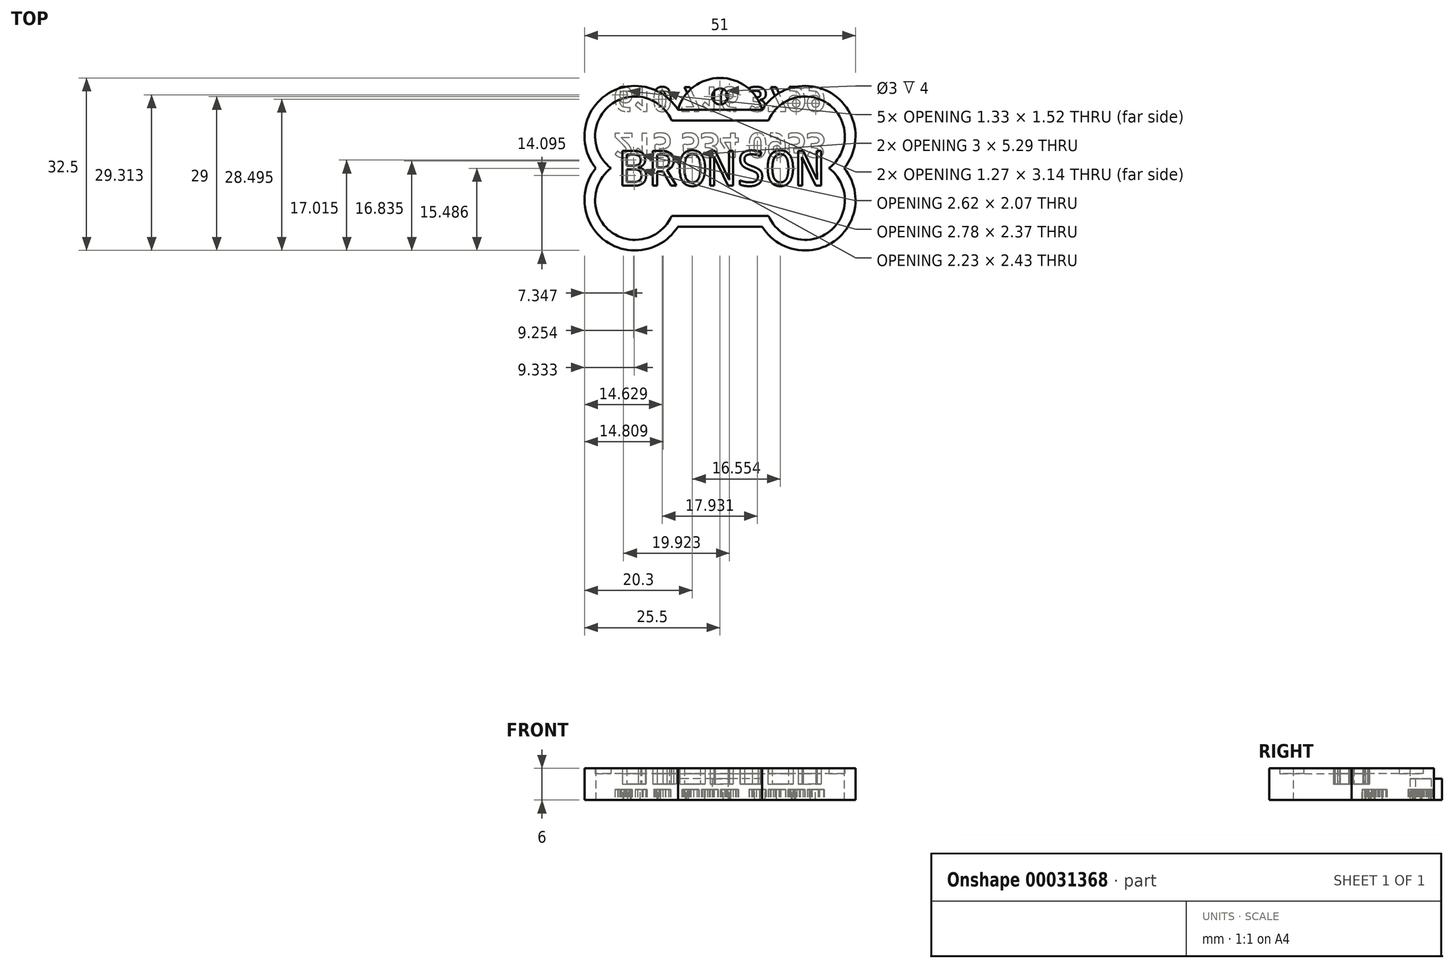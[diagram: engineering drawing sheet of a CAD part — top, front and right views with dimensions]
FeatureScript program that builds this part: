
annotation { "Feature Type Name" : "Feature", "Feature Type Description" : "" }
export const myFeature = defineFeature(function(context is Context, id is Id, definition is map)
    precondition{}
    {
        {
            var Q0;
            Q0=qCreatedBy(makeId("Top.planeOp"),FACE);
            var sketch = newSketch(context, id + "F0", { "sketchPlane" : qUnion([Q0])});
            skArc(sketch, "E0", {"start": v(-9.13, 9) * mm, "mid": v(-20.65, 11.88) * mm, "end": v(-20.5, 0) * mm});
            skLineSegment(sketch, "E1", {"start": v(0, 0) * mm, "end": v(0, -53.38) * mm, "construction": true});
            skLineSegment(sketch, "E2", {"start": v(0, 0) * mm, "end": v(-83.47, 0) * mm, "construction": true});
            skLineSegment(sketch, "E3", {"start": v(-9.13, 9) * mm, "end": v(0, 9) * mm});
            skArc(sketch, "E4.MirrorC", {"start": v(-9.13, -9) * mm, "mid": v(-20.65, -11.88) * mm, "end": v(-20.5, 0) * mm});
            skLineSegment(sketch, "E5.MirrorCS", {"start": v(-9.13, -9) * mm, "end": v(0, -9) * mm});
            skLineSegment(sketch, "E6.MirrorCS", {"start": v(9.13, 9) * mm, "end": v(0, 9) * mm});
            skLineSegment(sketch, "E7.MirrorCS", {"start": v(9.13, -9) * mm, "end": v(0, -9) * mm});
            skArc(sketch, "E8.MirrorC", {"start": v(9.13, -9) * mm, "mid": v(20.65, -11.88) * mm, "end": v(20.5, 0) * mm});
            skArc(sketch, "E9.MirrorC", {"start": v(9.13, 9) * mm, "mid": v(20.65, 11.88) * mm, "end": v(20.5, 0) * mm});
            skArc(sketch, "E10.0", {"start": v(7.92, 11) * mm, "mid": v(21.51, 13.74) * mm, "end": v(23.37, 0) * mm});
            skArc(sketch, "E10.1", {"start": v(7.92, -11) * mm, "mid": v(21.51, -13.74) * mm, "end": v(23.37, 0) * mm});
            skLineSegment(sketch, "E10.2", {"start": v(7.92, -11) * mm, "end": v(0, -11) * mm});
            skLineSegment(sketch, "E10.3", {"start": v(-7.92, -11) * mm, "end": v(0, -11) * mm});
            skArc(sketch, "E10.4", {"start": v(-7.92, -11) * mm, "mid": v(-21.51, -13.74) * mm, "end": v(-23.37, 0) * mm});
            skLineSegment(sketch, "E10.5", {"start": v(7.92, 11) * mm, "end": v(0, 11) * mm});
            skArc(sketch, "E10.6", {"start": v(-7.92, 11) * mm, "mid": v(-21.51, 13.74) * mm, "end": v(-23.37, 0) * mm});
            skLineSegment(sketch, "E10.7", {"start": v(-7.92, 11) * mm, "end": v(0, 11) * mm});
            skArc(sketch, "E11", {"start": v(7.92, 11) * mm, "mid": v(0, 17) * mm, "end": v(-7.92, 11) * mm});
            skLineSegment(sketch, "E12.bottom", {"start": v(-16, 6) * mm, "end": v(16, 6) * mm, "construction": true});
            skLineSegment(sketch, "E12.top", {"start": v(-16, -6) * mm, "end": v(16, -6) * mm, "construction": true});
            skLineSegment(sketch, "E12.left", {"start": v(-16, 6) * mm, "end": v(-16, -6) * mm, "construction": true});
            skLineSegment(sketch, "E12.right", {"start": v(16, 6) * mm, "end": v(16, -6) * mm, "construction": true});
            skPoint(sketch, "E13", {"position": v(0, 13.5) * mm});
            skSolve(sketch);
        }
        {
            var Q0;
            Q0=makeQuery(id+"F0.imprint","IMPRINT",FACE,{"disambiguationData":[TD([[makeQuery(id+"F0.imprint","IMPRINT",EDGE,{"derivedFrom":sQuery(id+"F0.wireOp",EDGE,"E0")}),-1.0]])]});
            extrude(context, id + "F1", {"entities" : qUnion([Q0]), "offsetDistance" : 25 * mm, "depth" : 6 * mm});
        }
        {
            var Q0;
            Q0=makeQuery(id+"F0.imprint","IMPRINT",FACE,{"disambiguationData":[TD([[makeQuery(id+"F0.imprint","IMPRINT",EDGE,{"derivedFrom":sQuery(id+"F0.wireOp",EDGE,"E10.5")}),-1.0]])]});
            extrude(context, id + "F2", {"entities" : qUnion([Q0]), "operationType" : NewBodyOperationType.ADD, "offsetDistance" : 25 * mm, "depth" : 4 * mm});
        }
        {
            var Q0;
            Q0=sQuery(id+"F0.wireOp",VERTEX,"E13");
            var Q1;
            Q1=makeQuery(id+"F1.opExtrude","SWEPT_BODY",BODY,{"disambiguationData":[OSD([sQuery(id+"F0.wireOp",EDGE,"E0"),sQuery(id+"F0.wireOp",EDGE,"E3"),sQuery(id+"F0.wireOp",EDGE,"E4.MirrorC"),sQuery(id+"F0.wireOp",EDGE,"E5.MirrorCS"),sQuery(id+"F0.wireOp",EDGE,"E6.MirrorCS"),sQuery(id+"F0.wireOp",EDGE,"E7.MirrorCS"),sQuery(id+"F0.wireOp",EDGE,"E8.MirrorC"),sQuery(id+"F0.wireOp",EDGE,"E9.MirrorC"),sQuery(id+"F0.wireOp",EDGE,"E10.0"),sQuery(id+"F0.wireOp",EDGE,"E10.1"),sQuery(id+"F0.wireOp",EDGE,"E10.2"),sQuery(id+"F0.wireOp",EDGE,"E10.3"),sQuery(id+"F0.wireOp",EDGE,"E10.4"),sQuery(id+"F0.wireOp",EDGE,"E10.6"),sQuery(id+"F0.wireOp",EDGE,"E11")])]});
            hole(context, id + "F3", {"style" : HoleStyle.SIMPLE, "holeDiameter" : 3 * mm, "endStyle" : HoleEndStyle.THROUGH, "oppositeDirection" : true, "locations" : qUnion([Q0]), "scope" : qUnion([Q1])});
        }
        {
            var Q0;
            Q0=makeQuery(id+"F0.imprint","IMPRINT",FACE,{"disambiguationData":[TD([[makeQuery(id+"F0.imprint","IMPRINT",EDGE,{"derivedFrom":sQuery(id+"F0.wireOp",EDGE,"E0")}),1.0]])]});
            extrude(context, id + "F4", {"entities" : qUnion([Q0]), "operationType" : NewBodyOperationType.ADD, "offsetDistance" : 25 * mm, "depth" : 3 * mm});
        }
        {
            var Q0;
            Q0=makeQuery(id+"F4.opExtrude","CAP_FACE",FACE,{"disambiguationData":[OSD([sQuery(id+"F0.wireOp",EDGE,"E0"),sQuery(id+"F0.wireOp",EDGE,"E3"),sQuery(id+"F0.wireOp",EDGE,"E4.MirrorC"),sQuery(id+"F0.wireOp",EDGE,"E5.MirrorCS"),sQuery(id+"F0.wireOp",EDGE,"E6.MirrorCS"),sQuery(id+"F0.wireOp",EDGE,"E7.MirrorCS"),sQuery(id+"F0.wireOp",EDGE,"E8.MirrorC"),sQuery(id+"F0.wireOp",EDGE,"E9.MirrorC")])],"isStart":false});
            var sketch = newSketch(context, id + "F5", { "sketchPlane" : qUnion([Q0])});
            skText(sketch, "E14", { "text": "BRONSON", "fontName": "DroidSansMono.ttf"});
            skPoint(sketch, "E15", {"position": v(-19, 0) * mm});
            const initialGuessF5  = {"E14": [-0.019, -0.0033, 1, 0, 0.00662]};
            skSetInitialGuess(sketch, initialGuessF5);
            skSolve(sketch);
        }
        {
            var Q0;
            Q0=makeQuery(id+"F5.imprint","IMPRINT",FACE,{"disambiguationData":[TD([[makeQuery(id+"F5.imprint","IMPRINT",EDGE,{"derivedFrom":sQuery(id+"F5.wireOp",EDGE,"E14.sketch_text.stroke-0")}),1.0]])]});
            var Q1;
            Q1=makeQuery(id+"F1.opExtrude","CAP_FACE",FACE,{"disambiguationData":[OSD([sQuery(id+"F0.wireOp",EDGE,"E0"),sQuery(id+"F0.wireOp",EDGE,"E3"),sQuery(id+"F0.wireOp",EDGE,"E4.MirrorC"),sQuery(id+"F0.wireOp",EDGE,"E5.MirrorCS"),sQuery(id+"F0.wireOp",EDGE,"E6.MirrorCS"),sQuery(id+"F0.wireOp",EDGE,"E7.MirrorCS"),sQuery(id+"F0.wireOp",EDGE,"E8.MirrorC"),sQuery(id+"F0.wireOp",EDGE,"E9.MirrorC"),sQuery(id+"F0.wireOp",EDGE,"E10.0"),sQuery(id+"F0.wireOp",EDGE,"E10.1"),sQuery(id+"F0.wireOp",EDGE,"E10.2"),sQuery(id+"F0.wireOp",EDGE,"E10.3"),sQuery(id+"F0.wireOp",EDGE,"E10.4"),sQuery(id+"F0.wireOp",EDGE,"E10.5"),sQuery(id+"F0.wireOp",EDGE,"E10.6"),sQuery(id+"F0.wireOp",EDGE,"E10.7")])],"isStart":false});
            extrude(context, id + "F6", {"entities" : qUnion([Q0]), "operationType" : NewBodyOperationType.ADD, "endBoundEntityFace" : qUnion([Q1]), "offsetDistance" : 25 * mm, "depth" : 2 * mm});
        }
        {
            var Q0;
            Q0 = qSketchRegion(id + "F5", true);
            var Q1;
            Q1=makeQuery(id+"F1.opExtrude","CAP_FACE",FACE,{"disambiguationData":[OSD([sQuery(id+"F0.wireOp",EDGE,"E0"),sQuery(id+"F0.wireOp",EDGE,"E3"),sQuery(id+"F0.wireOp",EDGE,"E4.MirrorC"),sQuery(id+"F0.wireOp",EDGE,"E5.MirrorCS"),sQuery(id+"F0.wireOp",EDGE,"E6.MirrorCS"),sQuery(id+"F0.wireOp",EDGE,"E7.MirrorCS"),sQuery(id+"F0.wireOp",EDGE,"E8.MirrorC"),sQuery(id+"F0.wireOp",EDGE,"E9.MirrorC"),sQuery(id+"F0.wireOp",EDGE,"E10.0"),sQuery(id+"F0.wireOp",EDGE,"E10.1"),sQuery(id+"F0.wireOp",EDGE,"E10.2"),sQuery(id+"F0.wireOp",EDGE,"E10.3"),sQuery(id+"F0.wireOp",EDGE,"E10.4"),sQuery(id+"F0.wireOp",EDGE,"E10.5"),sQuery(id+"F0.wireOp",EDGE,"E10.6"),sQuery(id+"F0.wireOp",EDGE,"E10.7")])],"isStart":false});
            extrude(context, id + "F7", {"entities" : qUnion([Q0]), "endBound" : BoundingType.UP_TO_SURFACE, "depth" : 2 * mm, "endBoundEntityFace" : qUnion([Q1]), "offsetDistance" : 25 * mm});
        }
        {
            var Q0;
            {var subQ0=sQuery(id+"F0.wireOp",EDGE,"E9.MirrorC");var subQ1=sQuery(id+"F0.wireOp",EDGE,"E8.MirrorC");var subQ2=sQuery(id+"F0.wireOp",EDGE,"E7.MirrorCS");var subQ3=sQuery(id+"F0.wireOp",EDGE,"E6.MirrorCS");var subQ4=sQuery(id+"F0.wireOp",EDGE,"E5.MirrorCS");var subQ5=sQuery(id+"F0.wireOp",EDGE,"E4.MirrorC");var subQ6=sQuery(id+"F0.wireOp",EDGE,"E3");var subQ7=sQuery(id+"F0.wireOp",EDGE,"E0");var subQ8=sQuery(id+"F0.wireOp",EDGE,"E10.7");var subQ9=sQuery(id+"F0.wireOp",EDGE,"E10.5");Q0=makeQuery(id+"F4.boolean.opBoolean","MERGE",FACE,{"derivedFrom":[makeQuery(id+"F2.boolean.opBoolean","MERGE",FACE,{"derivedFrom":[makeQuery(id+"F1.opExtrude","CAP_FACE",FACE,{"disambiguationData":[OSD([subQ7,subQ6,subQ5,subQ4,subQ3,subQ2,subQ1,subQ0,sQuery(id+"F0.wireOp",EDGE,"E10.0"),sQuery(id+"F0.wireOp",EDGE,"E10.1"),sQuery(id+"F0.wireOp",EDGE,"E10.2"),sQuery(id+"F0.wireOp",EDGE,"E10.3"),sQuery(id+"F0.wireOp",EDGE,"E10.4"),subQ9,sQuery(id+"F0.wireOp",EDGE,"E10.6"),subQ8])],"isStart":true}),makeQuery(id+"F2.opExtrude","CAP_FACE",FACE,{"disambiguationData":[OSD([subQ9,subQ8,sQuery(id+"F0.wireOp",EDGE,"E11")])],"isStart":true})]}),makeQuery(id+"F4.opExtrude","CAP_FACE",FACE,{"disambiguationData":[OSD([subQ7,subQ6,subQ5,subQ4,subQ3,subQ2,subQ1,subQ0])],"isStart":true})]});}
            var sketch = newSketch(context, id + "F8", { "sketchPlane" : qUnion([Q0])});
            skText(sketch, "E16", { "text": "215 534 0953\n610 716 3799", "fontName": "NotoSans-Bold.ttf"});
            const initialGuessF8  = {"E16": [-0.02, -0.00659, 1, 0, 0.0046]};
            skSetInitialGuess(sketch, initialGuessF8);
            skSolve(sketch);
        }
        {
            var Q0;
            Q0 = qSketchRegion(id + "F8", true);
            extrude(context, id + "F9", {"entities" : qUnion([Q0]), "operationType" : NewBodyOperationType.REMOVE, "oppositeDirection" : true, "depth" : 2 * mm, "offsetDistance" : 25 * mm});
        }
        {
            var Q0;
            Q0 = qSketchRegion(id + "F8", true);
            extrude(context, id + "F10", {"entities" : qUnion([Q0]), "oppositeDirection" : true, "depth" : 2 * mm, "offsetDistance" : 25 * mm});
        }
    });
